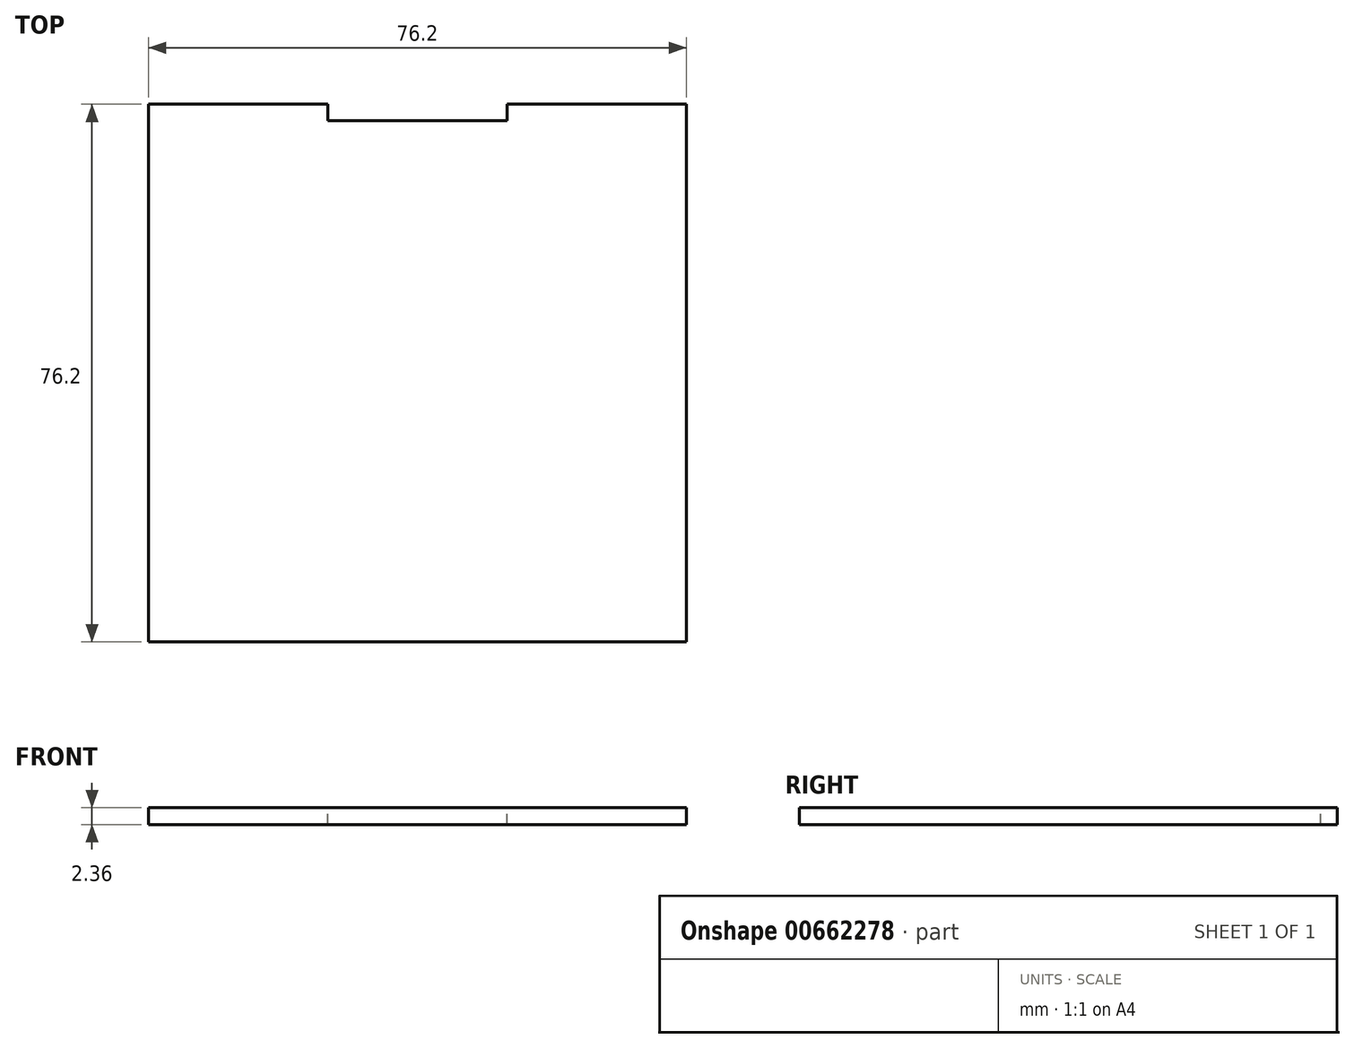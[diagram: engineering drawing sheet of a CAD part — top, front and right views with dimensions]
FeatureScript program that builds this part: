
annotation { "Feature Type Name" : "Feature", "Feature Type Description" : "" }
export const myFeature = defineFeature(function(context is Context, id is Id, definition is map)
    precondition{}
    {
        {
            var Q0;
            Q0=qCreatedBy(makeId("Top.planeOp"),FACE);
            var sketch = newSketch(context, id + "F0", { "sketchPlane" : qUnion([Q0])});
            skLineSegment(sketch, "E0.bottom", {"start": v(38.1, -38.1) * mm, "end": v(-38.1, -38.1) * mm});
            skLineSegment(sketch, "E0.top", {"start": v(38.1, 38.1) * mm, "end": v(-38.1, 38.1) * mm});
            skLineSegment(sketch, "E0.left", {"start": v(38.1, -38.1) * mm, "end": v(38.1, 38.1) * mm});
            skLineSegment(sketch, "E0.right", {"start": v(-38.1, -38.1) * mm, "end": v(-38.1, 38.1) * mm});
            skPoint(sketch, "E0.middle", {"position": v(0, 0) * mm});
            skSolve(sketch);
        }
        {
            var Q0;
            Q0 = qSketchRegion(id + "F0", true);
            extrude(context, id + "F1", {"entities" : qUnion([Q0]), "depth" : 2.36 * mm, "offsetDistance" : 25.4 * mm});
        }
        {
            var Q0;
            Q0=makeQuery(id+"F1.opExtrude","CAP_FACE",FACE,{"disambiguationData":[OSD([sQuery(id+"F0.wireOp",EDGE,"E0.bottom"),sQuery(id+"F0.wireOp",EDGE,"E0.top"),sQuery(id+"F0.wireOp",EDGE,"E0.left"),sQuery(id+"F0.wireOp",EDGE,"E0.right")])],"isStart":false});
            var sketch = newSketch(context, id + "F2", { "sketchPlane" : qUnion([Q0])});
            skLineSegment(sketch, "E1.bottom", {"start": v(-12.7, 38.1) * mm, "end": v(12.7, 38.1) * mm});
            skLineSegment(sketch, "E1.top", {"start": v(-12.7, 35.74) * mm, "end": v(12.7, 35.74) * mm});
            skLineSegment(sketch, "E1.left", {"start": v(-12.7, 38.1) * mm, "end": v(-12.7, 35.74) * mm});
            skLineSegment(sketch, "E1.right", {"start": v(12.7, 38.1) * mm, "end": v(12.7, 35.74) * mm});
            skSolve(sketch);
        }
        {
            var Q0;
            Q0=qCreatedBy(makeId("Right.planeOp"),FACE);
            var sketch = newSketch(context, id + "F3", { "sketchPlane" : qUnion([Q0])});
            skLineSegment(sketch, "E2", {"start": v(0, 0) * mm, "end": v(0, 36.5) * mm});
            skSolve(sketch);
        }
        {
            var Q0;
            Q0=makeQuery(id+"F2.imprint","IMPRINT",FACE,{"disambiguationData":[TD([[makeQuery(id+"F2.imprint","IMPRINT",EDGE,{"derivedFrom":sQuery(id+"F2.wireOp",EDGE,"E1.bottom")}),1.0]])]});
            extrude(context, id + "F4", {"entities" : qUnion([Q0]), "operationType" : NewBodyOperationType.REMOVE, "oppositeDirection" : true, "depth" : 25.4 * mm, "offsetDistance" : 25.4 * mm});
        }
    });
